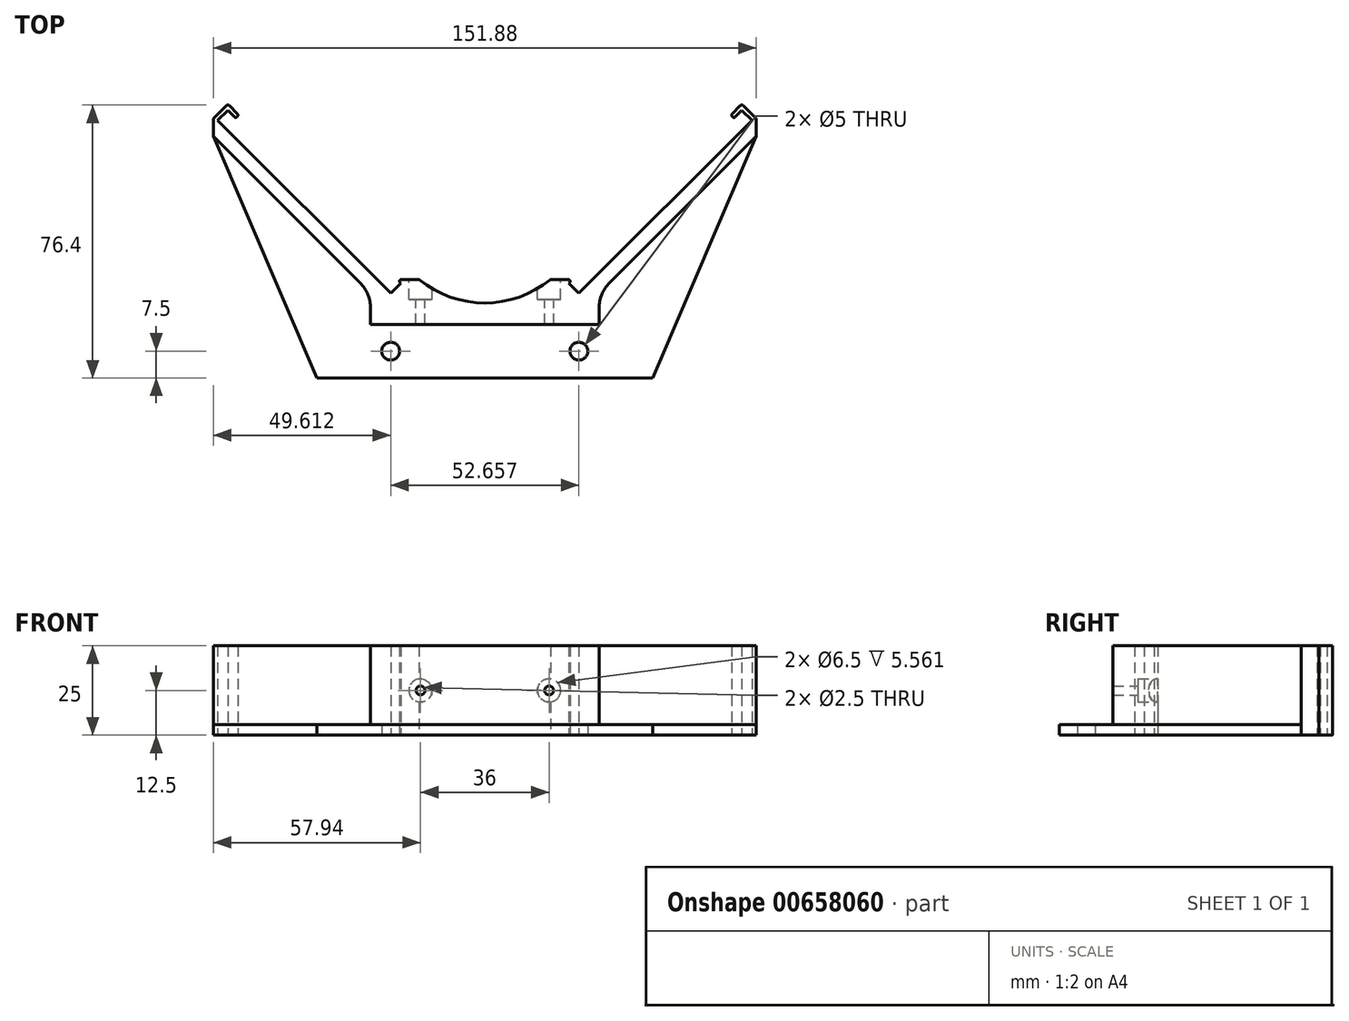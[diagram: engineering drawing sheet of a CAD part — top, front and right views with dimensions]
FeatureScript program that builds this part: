
annotation { "Feature Type Name" : "Feature", "Feature Type Description" : "" }
export const myFeature = defineFeature(function(context is Context, id is Id, definition is map)
    precondition{}
    {
        {
            var Q0;
            Q0=qCreatedBy(makeId("Top.planeOp"),FACE);
            var sketch = newSketch(context, id + "F0", { "sketchPlane" : qUnion([Q0])});
            skLineSegment(sketch, "E0.MirrorCS", {"start": v(31.99, 0) * mm, "end": v(0, 0) * mm});
            skLineSegment(sketch, "E1.MirrorCS", {"start": v(26.33, 8.67) * mm, "end": v(23.5, 11.5) * mm});
            skCircle(sketch, "E2", {"center": v(0, 35) * mm, "radius": 23.5 * mm});
            skCircle(sketch, "E3", {"center": v(0, 35) * mm, "radius": 29 * mm});
            skArc(sketch, "E4.MirrorCS", {"start": v(31.99, 4.53) * mm, "mid": v(32.75, 8.36) * mm, "end": v(34.91, 11.6) * mm});
            skLineSegment(sketch, "E5.MirrorCS", {"start": v(31.99, 4.53) * mm, "end": v(31.99, 0) * mm});
            skLineSegment(sketch, "E6.MirrorCS", {"start": v(73.33, 55.67) * mm, "end": v(70.5, 58.5) * mm, "construction": true});
            skLineSegment(sketch, "E7.MirrorCS", {"start": v(34.91, 11.6) * mm, "end": v(75.94, 52.63) * mm});
            skLineSegment(sketch, "E8.MirrorCS", {"start": v(73.33, 55.67) * mm, "end": v(26.33, 8.67) * mm});
            skLineSegment(sketch, "E9.MirrorCS", {"start": v(0, 58.5) * mm, "end": v(70.5, 58.5) * mm, "construction": true});
            skLineSegment(sketch, "E10.MirrorCS", {"start": v(23.5, 35) * mm, "end": v(23.5, 11.5) * mm, "construction": true});
            skLineSegment(sketch, "E11.MirrorCS", {"start": v(0, 11.5) * mm, "end": v(23.5, 11.5) * mm, "construction": true});
            skLineSegment(sketch, "E12", {"start": v(73.33, 55.67) * mm, "end": v(74.74, 57.09) * mm});
            skLineSegment(sketch, "E13", {"start": v(74.74, 57.09) * mm, "end": v(71.91, 59.91) * mm});
            skLineSegment(sketch, "E14", {"start": v(71.91, 59.91) * mm, "end": v(70.5, 58.5) * mm});
            skLineSegment(sketch, "E15", {"start": v(70.5, 58.5) * mm, "end": v(70.08, 58.08) * mm});
            skLineSegment(sketch, "E16", {"start": v(69.38, 58.08) * mm, "end": v(69.24, 58.23) * mm});
            skLineSegment(sketch, "E17", {"start": v(69.24, 58.93) * mm, "end": v(71.56, 61.26) * mm});
            skLineSegment(sketch, "E18", {"start": v(72.27, 61.26) * mm, "end": v(75.94, 57.58) * mm});
            skLineSegment(sketch, "E19", {"start": v(23.5, 11.5) * mm, "end": v(23.7, 11.7) * mm});
            skLineSegment(sketch, "E20", {"start": v(23.35, 12.56) * mm, "end": v(18.37, 12.56) * mm});
            skPoint(sketch, "E21.visualSharp", {"position": v(24.56, 12.56) * mm});
            skArc(sketch, "E21.filletArc", {"start": v(23.7, 11.7) * mm, "mid": v(23.82, 12.25) * mm, "end": v(23.35, 12.56) * mm});
            skLineSegment(sketch, "E22", {"start": v(23.5, 11.5) * mm, "end": v(70.5, 58.5) * mm, "construction": true});
            skLineSegment(sketch, "E23", {"start": v(75.94, 57.58) * mm, "end": v(75.94, 52.63) * mm});
            skPoint(sketch, "E24.visualSharp", {"position": v(71.91, 61.61) * mm});
            skArc(sketch, "E24.filletArc", {"start": v(72.27, 61.26) * mm, "mid": v(71.91, 61.4) * mm, "end": v(71.56, 61.26) * mm});
            skPoint(sketch, "E25.visualSharp", {"position": v(68.88, 58.58) * mm});
            skArc(sketch, "E25.filletArc", {"start": v(69.24, 58.93) * mm, "mid": v(69.09, 58.58) * mm, "end": v(69.24, 58.23) * mm});
            skPoint(sketch, "E26.visualSharp", {"position": v(69.73, 57.73) * mm});
            skArc(sketch, "E26.filletArc", {"start": v(69.38, 58.08) * mm, "mid": v(69.73, 57.94) * mm, "end": v(70.08, 58.08) * mm});
            skArc(sketch, "E27.MirrorCS", {"start": v(-69.38, 58.08) * mm, "mid": v(-69.73, 57.94) * mm, "end": v(-70.08, 58.08) * mm});
            skLineSegment(sketch, "E28.MirrorCS", {"start": v(-70.5, 58.5) * mm, "end": v(-70.08, 58.08) * mm});
            skLineSegment(sketch, "E29.MirrorCS", {"start": v(-71.91, 59.91) * mm, "end": v(-70.5, 58.5) * mm});
            skArc(sketch, "E30.MirrorCS", {"start": v(-23.7, 11.7) * mm, "mid": v(-23.82, 12.25) * mm, "end": v(-23.35, 12.56) * mm});
            skArc(sketch, "E31.MirrorCS", {"start": v(-69.24, 58.93) * mm, "mid": v(-69.09, 58.58) * mm, "end": v(-69.24, 58.23) * mm});
            skLineSegment(sketch, "E32.MirrorCS", {"start": v(-23.5, 11.5) * mm, "end": v(-23.7, 11.7) * mm});
            skLineSegment(sketch, "E33.MirrorCS", {"start": v(-69.38, 58.08) * mm, "end": v(-69.24, 58.23) * mm});
            skLineSegment(sketch, "E34.MirrorCS", {"start": v(-26.33, 8.67) * mm, "end": v(-23.5, 11.5) * mm});
            skLineSegment(sketch, "E35.MirrorCS", {"start": v(-73.33, 55.67) * mm, "end": v(-74.74, 57.09) * mm});
            skLineSegment(sketch, "E36.MirrorCS", {"start": v(-73.33, 55.67) * mm, "end": v(-70.5, 58.5) * mm, "construction": true});
            skArc(sketch, "E37.MirrorCS", {"start": v(-72.27, 61.26) * mm, "mid": v(-71.91, 61.4) * mm, "end": v(-71.56, 61.26) * mm});
            skLineSegment(sketch, "E38.MirrorCS", {"start": v(-69.24, 58.93) * mm, "end": v(-71.56, 61.26) * mm});
            skLineSegment(sketch, "E39.MirrorCS", {"start": v(-74.74, 57.09) * mm, "end": v(-71.91, 59.91) * mm});
            skLineSegment(sketch, "E40.MirrorCS", {"start": v(-23.35, 12.56) * mm, "end": v(-18.37, 12.56) * mm});
            skLineSegment(sketch, "E41.MirrorCS", {"start": v(-72.27, 61.26) * mm, "end": v(-75.94, 57.58) * mm});
            skLineSegment(sketch, "E42.MirrorCS", {"start": v(0, 11.5) * mm, "end": v(-23.5, 11.5) * mm, "construction": true});
            skLineSegment(sketch, "E43.MirrorCS", {"start": v(-23.5, 35) * mm, "end": v(-23.5, 11.5) * mm, "construction": true});
            skLineSegment(sketch, "E44.MirrorCS", {"start": v(0, 58.5) * mm, "end": v(-70.5, 58.5) * mm, "construction": true});
            skLineSegment(sketch, "E45.MirrorCS", {"start": v(-34.91, 11.6) * mm, "end": v(-75.94, 52.63) * mm});
            skPoint(sketch, "E46.MirrorP", {"position": v(-71.91, 61.61) * mm});
            skLineSegment(sketch, "E47.MirrorCS", {"start": v(-75.94, 57.58) * mm, "end": v(-75.94, 52.63) * mm});
            skPoint(sketch, "E48.MirrorP", {"position": v(-69.73, 57.73) * mm});
            skLineSegment(sketch, "E49.MirrorCS", {"start": v(-23.5, 11.5) * mm, "end": v(-70.5, 58.5) * mm, "construction": true});
            skPoint(sketch, "E50.MirrorP", {"position": v(-68.88, 58.58) * mm});
            skArc(sketch, "E51.MirrorCS", {"start": v(-31.99, 4.53) * mm, "mid": v(-32.75, 8.36) * mm, "end": v(-34.91, 11.6) * mm});
            skPoint(sketch, "E52.MirrorP", {"position": v(-24.56, 12.56) * mm});
            skLineSegment(sketch, "E53.MirrorCS", {"start": v(-31.99, 0) * mm, "end": v(0, 0) * mm});
            skLineSegment(sketch, "E54.MirrorCS", {"start": v(-31.99, 4.53) * mm, "end": v(-31.99, 0) * mm});
            skLineSegment(sketch, "E55.MirrorCS", {"start": v(-73.33, 55.67) * mm, "end": v(-26.33, 8.67) * mm});
            skSolve(sketch);
        }
        {
            var Q0;
            Q0=makeQuery(id+"F0.imprint","IMPRINT",FACE,{"disambiguationData":[TD([[makeQuery(id+"F0.imprint","IMPRINT",EDGE,{"derivedFrom":sQuery(id+"F0.wireOp",EDGE,"E0.MirrorCS")}),-1.0]])]});
            extrude(context, id + "F1", {"entities" : qUnion([Q0]), "endBound" : BoundingType.SYMMETRIC, "depth" : 25 * mm, "offsetDistance" : 25 * mm});
        }
        {
            var Q0;
            Q0=qCreatedBy(makeId("Top.planeOp"),FACE);
            var sketch = newSketch(context, id + "F2", { "sketchPlane" : qUnion([Q0])});
            skLineSegment(sketch, "E56", {"start": v(-19.25, -4.8) * mm, "end": v(-16.75, -4.8) * mm});
            skLineSegment(sketch, "E57", {"start": v(-19.25, -4.8) * mm, "end": v(-19.25, 7) * mm});
            skLineSegment(sketch, "E58", {"start": v(-21.25, 7) * mm, "end": v(-19.25, 7) * mm});
            skLineSegment(sketch, "E59", {"start": v(-21.25, 7) * mm, "end": v(-21.25, 19.22) * mm});
            skLineSegment(sketch, "E60", {"start": v(-14.75, 19.22) * mm, "end": v(-21.25, 19.22) * mm});
            skLineSegment(sketch, "E61", {"start": v(-14.75, 19.22) * mm, "end": v(-14.75, 7) * mm});
            skLineSegment(sketch, "E62", {"start": v(-14.75, 7) * mm, "end": v(-16.75, 7) * mm});
            skLineSegment(sketch, "E63", {"start": v(-16.75, 7) * mm, "end": v(-16.75, -4.8) * mm});
            skLineSegment(sketch, "E64", {"start": v(-18, 19.22) * mm, "end": v(-18, -4.8) * mm});
            skSolve(sketch);
        }
        {
            var Q0;
            {var subQ0=sQuery(id+"F2.wireOp",EDGE,"E61");Q0=makeQuery(id+"F2.imprint","IMPRINT",FACE,{"disambiguationData":[TD([[makeQuery(id+"F2.imprint","IMPRINT",EDGE,{"derivedFrom":subQ0}),-1.0]])]});}
            var Q1;
            Q1=sQuery(id+"F2.wireOp",EDGE,"E64");
            revolve(context, id + "F3", {"entities" : qUnion([Q0]), "axis" : qUnion([Q1]), "revolveType" : RevolveType.FULL});
        }
        {
            var Q0;
            Q0=makeQuery(id+"F3.opRevolve","SWEPT_BODY",BODY,{"disambiguationData":[OSD([sQuery(id+"F2.wireOp",EDGE,"E56"),sQuery(id+"F2.wireOp",EDGE,"E60"),sQuery(id+"F2.wireOp",EDGE,"E61"),sQuery(id+"F2.wireOp",EDGE,"E62"),sQuery(id+"F2.wireOp",EDGE,"E63"),sQuery(id+"F2.wireOp",EDGE,"E64")])]});
            var Q1;
            Q1=qCreatedBy(makeId("Right.planeOp"),FACE);
            mirror(context, id + "F4", {"entities" : qUnion([Q0]), "mirrorPlane" : qUnion([Q1])});
        }
        {
            var Q0;
            Q0=makeQuery(id+"F3.opRevolve","SWEPT_BODY",BODY,{"disambiguationData":[OSD([sQuery(id+"F2.wireOp",EDGE,"E56"),sQuery(id+"F2.wireOp",EDGE,"E60"),sQuery(id+"F2.wireOp",EDGE,"E61"),sQuery(id+"F2.wireOp",EDGE,"E62"),sQuery(id+"F2.wireOp",EDGE,"E63"),sQuery(id+"F2.wireOp",EDGE,"E64")])]});
            var Q1;
            Q1=makeQuery(id+"F4.opPattern","COPY",BODY,{"derivedFrom":makeQuery(id+"F3.opRevolve","SWEPT_BODY",BODY,{"disambiguationData":[OSD([sQuery(id+"F2.wireOp",EDGE,"E56"),sQuery(id+"F2.wireOp",EDGE,"E60"),sQuery(id+"F2.wireOp",EDGE,"E61"),sQuery(id+"F2.wireOp",EDGE,"E62"),sQuery(id+"F2.wireOp",EDGE,"E63"),sQuery(id+"F2.wireOp",EDGE,"E64")])]}),"instanceName":"1"});
            var Q2;
            Q2=makeQuery(id+"F1.opExtrude","SWEPT_BODY",BODY,{"disambiguationData":[OSD([sQuery(id+"F0.wireOp",EDGE,"mkPKdniT-3bTg-n2zG-aNhe-nb5uCVJNovAu"),sQuery(id+"F0.wireOp",EDGE,"HuXQuEfz-Ws79-Lh7T-rxAL-mS0iCcUPfkBI"),sQuery(id+"F0.wireOp",EDGE,"Of7c2Ze6-LK7I-7pHe-cgwF-AvSWVdfIppal"),sQuery(id+"F0.wireOp",EDGE,"tdJDa12d-ZkFL-cPxZ-ZaZg-ISqDy0VeDeJR"),sQuery(id+"F0.wireOp",EDGE,"7l4LQ2dQ-QMhm-yQ98-GF7P-efJXpNuXIUlh"),sQuery(id+"F0.wireOp",EDGE,"4TUXZ2cs-jJPs-KIrJ-8jVw-TdqoFKcPvF7V"),sQuery(id+"F0.wireOp",EDGE,"E0.MirrorCS"),sQuery(id+"F0.wireOp",EDGE,"E1.MirrorCS"),sQuery(id+"F0.wireOp",EDGE,"bbOgV28H-PnXN-hk5e-9UHS-10X6mPLKgAY1"),sQuery(id+"F0.wireOp",EDGE,"E3"),sQuery(id+"F0.wireOp",EDGE,"xSyj21qh-FkRM-kMNU-Ydk0-I15ZGge8kWRO"),sQuery(id+"F0.wireOp",EDGE,"XtPQco39-DlP2-0unC-3IuJ-ViVnIXh9jFDL"),sQuery(id+"F0.wireOp",EDGE,"MZcQCY4g-NNFv-us4V-q7Cd-x8ar5fMTQvOq"),sQuery(id+"F0.wireOp",EDGE,"XKHQfTiF-0IDv-lvFl-kf71-XrSovQtoVNQP"),sQuery(id+"F0.wireOp",EDGE,"767ab26a-10a8-4ccf-b961-a32f313f0f3c.filletArc"),sQuery(id+"F0.wireOp",EDGE,"fb36068b-e9e9-457a-af9a-3dc0c5280496.filletArc"),sQuery(id+"F0.wireOp",EDGE,"e73da256-8a8a-4822-a508-ac1716414217.filletArc"),sQuery(id+"F0.wireOp",EDGE,"fdf2bc82-2aed-4963-bd4a-d64e87e19be10.MirrorCS"),sQuery(id+"F0.wireOp",EDGE,"fdf2bc82-2aed-4963-bd4a-d64e87e19be11.MirrorCS"),sQuery(id+"F0.wireOp",EDGE,"fdf2bc82-2aed-4963-bd4a-d64e87e19be12.MirrorCS"),sQuery(id+"F0.wireOp",EDGE,"fdf2bc82-2aed-4963-bd4a-d64e87e19be13.MirrorCS"),sQuery(id+"F0.wireOp",EDGE,"fdf2bc82-2aed-4963-bd4a-d64e87e19be14.MirrorCS"),sQuery(id+"F0.wireOp",EDGE,"fdf2bc82-2aed-4963-bd4a-d64e87e19be15.MirrorCS"),sQuery(id+"F0.wireOp",EDGE,"fdf2bc82-2aed-4963-bd4a-d64e87e19be18.MirrorCS"),sQuery(id+"F0.wireOp",EDGE,"fdf2bc82-2aed-4963-bd4a-d64e87e19be19.MirrorCS"),sQuery(id+"F0.wireOp",EDGE,"971688f7-6b3f-4f67-b2ec-8487d99c1ea30.MirrorCS"),sQuery(id+"F0.wireOp",EDGE,"971688f7-6b3f-4f67-b2ec-8487d99c1ea31.MirrorCS"),sQuery(id+"F0.wireOp",EDGE,"971688f7-6b3f-4f67-b2ec-8487d99c1ea32.MirrorCS"),sQuery(id+"F0.wireOp",EDGE,"7wOiaxwq-i9UI-vNx9-MGfG-lg538Gu5jbAO"),sQuery(id+"F0.wireOp",EDGE,"3a69b874-7704-4ae9-b641-182b72aa6ac8.filletArc"),sQuery(id+"F0.wireOp",EDGE,"E4.MirrorCS"),sQuery(id+"F0.wireOp",EDGE,"E5.MirrorCS"),sQuery(id+"F0.wireOp",EDGE,"117a50da-0f29-49d6-a308-a8a8691b76a70.MirrorCS")])]});
            booleanBodies(context, id + "F5", {"operationType" : BooleanOperationType.SUBTRACTION, "tools" : qUnion([Q0, Q1]), "targets" : qUnion([Q2])});
        }
        {
            var Q0;
            Q0=makeQuery(id+"F1.opExtrude","CAP_FACE",FACE,{"disambiguationData":[OSD([sQuery(id+"F0.wireOp",EDGE,"mkPKdniT-3bTg-n2zG-aNhe-nb5uCVJNovAu"),sQuery(id+"F0.wireOp",EDGE,"Of7c2Ze6-LK7I-7pHe-cgwF-AvSWVdfIppal"),sQuery(id+"F0.wireOp",EDGE,"tdJDa12d-ZkFL-cPxZ-ZaZg-ISqDy0VeDeJR"),sQuery(id+"F0.wireOp",EDGE,"7l4LQ2dQ-QMhm-yQ98-GF7P-efJXpNuXIUlh"),sQuery(id+"F0.wireOp",EDGE,"4TUXZ2cs-jJPs-KIrJ-8jVw-TdqoFKcPvF7V"),sQuery(id+"F0.wireOp",EDGE,"E0.MirrorCS"),sQuery(id+"F0.wireOp",EDGE,"E1.MirrorCS"),sQuery(id+"F0.wireOp",EDGE,"bbOgV28H-PnXN-hk5e-9UHS-10X6mPLKgAY1"),sQuery(id+"F0.wireOp",EDGE,"E3"),sQuery(id+"F0.wireOp",EDGE,"xSyj21qh-FkRM-kMNU-Ydk0-I15ZGge8kWRO"),sQuery(id+"F0.wireOp",EDGE,"XtPQco39-DlP2-0unC-3IuJ-ViVnIXh9jFDL"),sQuery(id+"F0.wireOp",EDGE,"MZcQCY4g-NNFv-us4V-q7Cd-x8ar5fMTQvOq"),sQuery(id+"F0.wireOp",EDGE,"XKHQfTiF-0IDv-lvFl-kf71-XrSovQtoVNQP"),sQuery(id+"F0.wireOp",EDGE,"767ab26a-10a8-4ccf-b961-a32f313f0f3c.filletArc"),sQuery(id+"F0.wireOp",EDGE,"fb36068b-e9e9-457a-af9a-3dc0c5280496.filletArc"),sQuery(id+"F0.wireOp",EDGE,"e73da256-8a8a-4822-a508-ac1716414217.filletArc"),sQuery(id+"F0.wireOp",EDGE,"fdf2bc82-2aed-4963-bd4a-d64e87e19be10.MirrorCS"),sQuery(id+"F0.wireOp",EDGE,"fdf2bc82-2aed-4963-bd4a-d64e87e19be11.MirrorCS"),sQuery(id+"F0.wireOp",EDGE,"fdf2bc82-2aed-4963-bd4a-d64e87e19be12.MirrorCS"),sQuery(id+"F0.wireOp",EDGE,"fdf2bc82-2aed-4963-bd4a-d64e87e19be13.MirrorCS"),sQuery(id+"F0.wireOp",EDGE,"fdf2bc82-2aed-4963-bd4a-d64e87e19be14.MirrorCS"),sQuery(id+"F0.wireOp",EDGE,"fdf2bc82-2aed-4963-bd4a-d64e87e19be15.MirrorCS"),sQuery(id+"F0.wireOp",EDGE,"fdf2bc82-2aed-4963-bd4a-d64e87e19be19.MirrorCS"),sQuery(id+"F0.wireOp",EDGE,"971688f7-6b3f-4f67-b2ec-8487d99c1ea30.MirrorCS"),sQuery(id+"F0.wireOp",EDGE,"971688f7-6b3f-4f67-b2ec-8487d99c1ea32.MirrorCS"),sQuery(id+"F0.wireOp",EDGE,"7wOiaxwq-i9UI-vNx9-MGfG-lg538Gu5jbAO"),sQuery(id+"F0.wireOp",EDGE,"3a69b874-7704-4ae9-b641-182b72aa6ac8.filletArc"),sQuery(id+"F0.wireOp",EDGE,"E4.MirrorCS"),sQuery(id+"F0.wireOp",EDGE,"E5.MirrorCS"),sQuery(id+"F0.wireOp",EDGE,"BgdLgmDP-1JpV-e2se-374d-a0HuRuLxEz3o"),sQuery(id+"F0.wireOp",EDGE,"odZ0BiTm-a6Wr-Ix6h-Mg3p-L72HwnXL3fAE"),sQuery(id+"F0.wireOp",EDGE,"fDvvIa8O-5rfG-VUHf-cS0a-5YTXraIC0XgI"),sQuery(id+"F0.wireOp",EDGE,"14cb47f2-67c6-4adb-8630-c180c8ddfe841.MirrorCS"),sQuery(id+"F0.wireOp",EDGE,"14cb47f2-67c6-4adb-8630-c180c8ddfe842.MirrorCS"),sQuery(id+"F0.wireOp",EDGE,"14cb47f2-67c6-4adb-8630-c180c8ddfe843.MirrorCS"),sQuery(id+"F0.wireOp",EDGE,"14cb47f2-67c6-4adb-8630-c180c8ddfe844.MirrorCS"),sQuery(id+"F0.wireOp",EDGE,"14cb47f2-67c6-4adb-8630-c180c8ddfe845.MirrorCS")])],"isStart":true});
            var sketch = newSketch(context, id + "F6", { "sketchPlane" : qUnion([Q0])});
            skLineSegment(sketch, "E65", {"start": v(0, 15) * mm, "end": v(46.99, 15) * mm});
            skLineSegment(sketch, "E66", {"start": v(31.99, 0) * mm, "end": v(46.99, 15) * mm, "construction": true});
            skLineSegment(sketch, "E67", {"start": v(0, 0) * mm, "end": v(0, 15) * mm});
            skLineSegment(sketch, "E68.MirrorCS", {"start": v(0, 15) * mm, "end": v(-46.99, 15) * mm});
            skLineSegment(sketch, "E69.MirrorCS", {"start": v(-75.94, -52.63) * mm, "end": v(-23.31, 0) * mm});
            skLineSegment(sketch, "E70.MirrorCS", {"start": v(-23.31, 0) * mm, "end": v(0, 0) * mm});
            skLineSegment(sketch, "E71.MirrorCS", {"start": v(-46.99, 15) * mm, "end": v(-75.94, -52.63) * mm});
            skLineSegment(sketch, "E72.MirrorCS", {"start": v(46.99, 15) * mm, "end": v(75.94, -52.63) * mm});
            skLineSegment(sketch, "E73.MirrorCS", {"start": v(23.31, 0) * mm, "end": v(0, 0) * mm});
            skLineSegment(sketch, "E74.MirrorCS", {"start": v(75.94, -52.63) * mm, "end": v(23.31, 0) * mm});
            skCircle(sketch, "E75", {"center": v(26.33, 7.5) * mm, "radius": 2.5 * mm});
            skCircle(sketch, "E76.MirrorC", {"center": v(-26.33, 7.5) * mm, "radius": 2.5 * mm});
            skSolve(sketch);
        }
        {
            var Q0;
            Q0=makeQuery(id+"F6.imprint","IMPRINT",FACE,{"disambiguationData":[TD([[makeQuery(id+"F6.imprint","IMPRINT",EDGE,{"derivedFrom":sQuery(id+"F6.wireOp",EDGE,"E67")}),-1.0]])]});
            var Q1;
            Q1=makeQuery(id+"F6.imprint","IMPRINT",FACE,{"disambiguationData":[TD([[makeQuery(id+"F6.imprint","IMPRINT",EDGE,{"derivedFrom":sQuery(id+"F6.wireOp",EDGE,"E67")}),1.0]])]});
            extrude(context, id + "F7", {"entities" : qUnion([Q0, Q1]), "operationType" : NewBodyOperationType.ADD, "oppositeDirection" : true, "depth" : 3 * mm, "offsetDistance" : 25 * mm});
        }
    });
